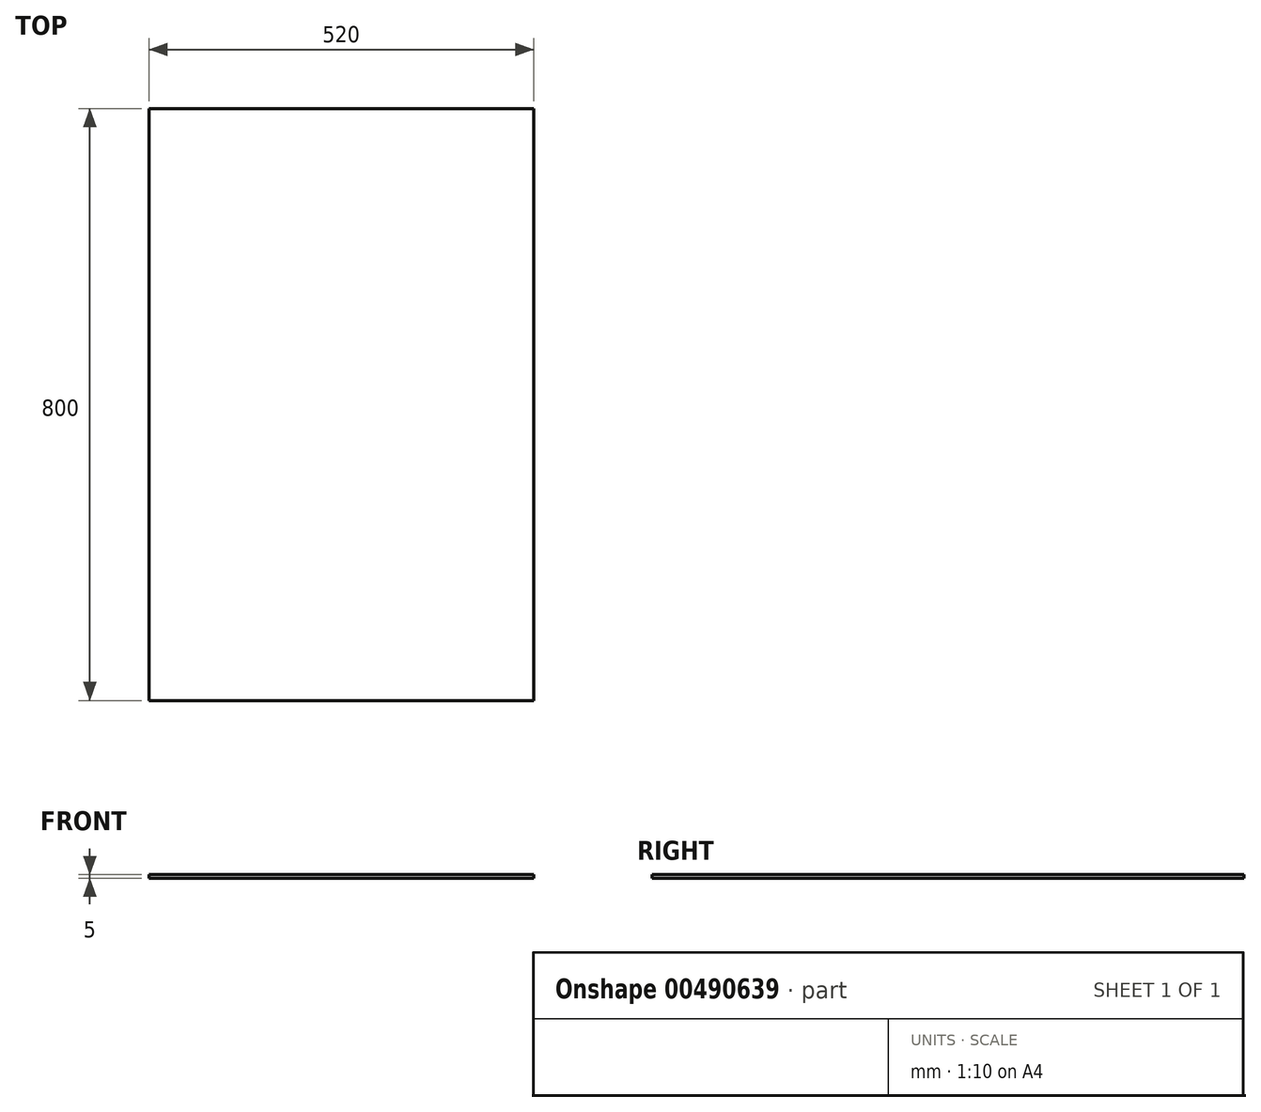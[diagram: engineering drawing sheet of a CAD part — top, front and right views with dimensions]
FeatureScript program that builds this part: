
annotation { "Feature Type Name" : "Feature", "Feature Type Description" : "" }
export const myFeature = defineFeature(function(context is Context, id is Id, definition is map)
    precondition{}
    {
        {
            var Q0;
            Q0=qCreatedBy(makeId("Top.planeOp"),FACE);
            var sketch = newSketch(context, id + "F0", { "sketchPlane" : qUnion([Q0])});
            skLineSegment(sketch, "E0.bottom", {"start": v(0, 0) * mm, "end": v(-520, 0) * mm});
            skLineSegment(sketch, "E0.top", {"start": v(0, -800) * mm, "end": v(-520, -800) * mm});
            skLineSegment(sketch, "E0.left", {"start": v(0, 0) * mm, "end": v(0, -800) * mm});
            skLineSegment(sketch, "E0.right", {"start": v(-520, 0) * mm, "end": v(-520, -800) * mm});
            skSolve(sketch);
        }
        {
            var Q0;
            Q0=makeQuery(id+"F0.imprint","IMPRINT",FACE,{"disambiguationData":[TD([[makeQuery(id+"F0.imprint","IMPRINT",EDGE,{"derivedFrom":sQuery(id+"F0.wireOp",EDGE,"E0.bottom")}),1.0]])]});
            extrude(context, id + "F1", {"entities" : qUnion([Q0]), "depth" : 5 * mm});
        }
    });
